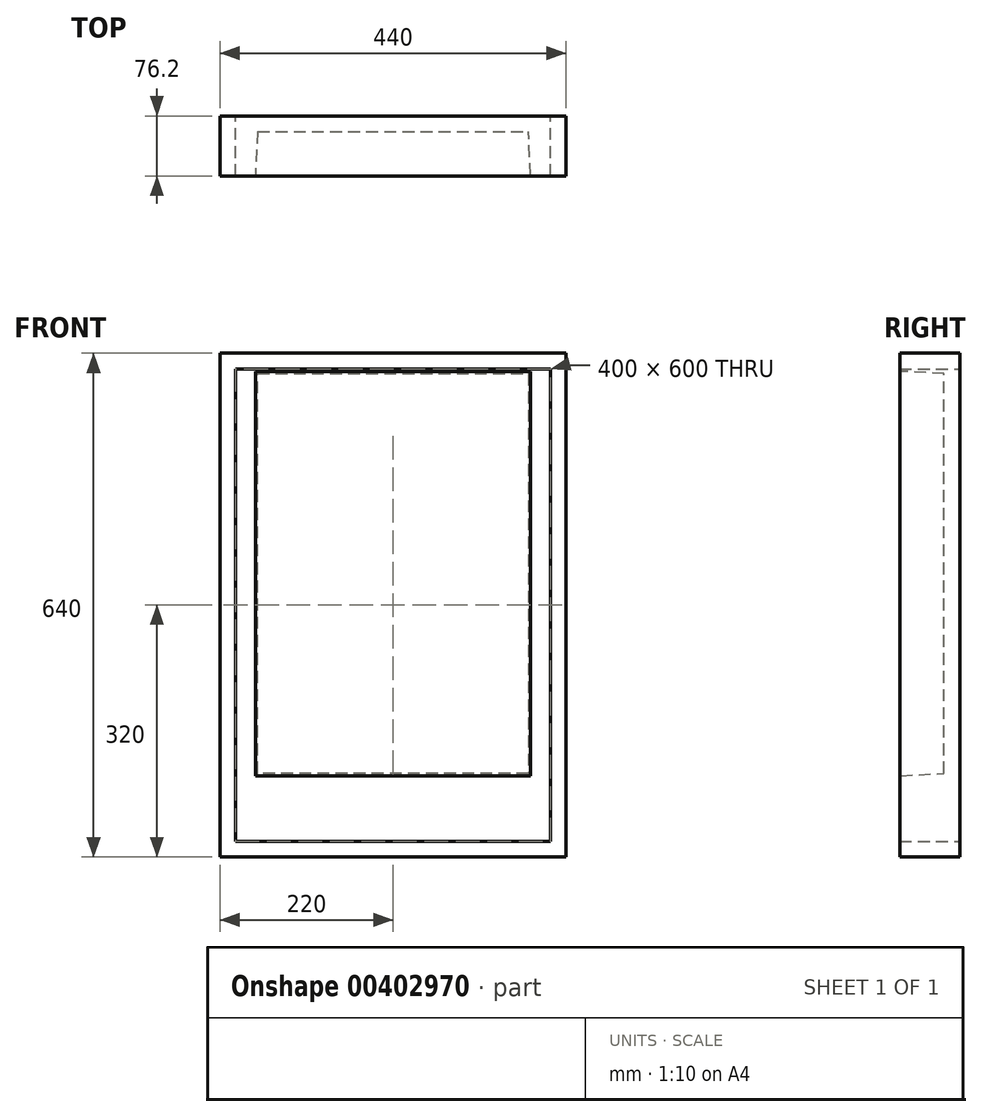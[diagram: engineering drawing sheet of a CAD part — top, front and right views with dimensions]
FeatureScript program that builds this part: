
annotation { "Feature Type Name" : "Feature", "Feature Type Description" : "" }
export const myFeature = defineFeature(function(context is Context, id is Id, definition is map)
    precondition{}
    {
        {
            var Q0;
            Q0=qCreatedBy(makeId("Front.planeOp"),FACE);
            var sketch = newSketch(context, id + "F0", { "sketchPlane" : qUnion([Q0])});
            skLineSegment(sketch, "E0.bottom", {"start": v(-220, 320) * mm, "end": v(220, 320) * mm});
            skLineSegment(sketch, "E0.top", {"start": v(-220, -320) * mm, "end": v(220, -320) * mm});
            skLineSegment(sketch, "E0.left", {"start": v(-220, 320) * mm, "end": v(-220, -320) * mm});
            skLineSegment(sketch, "E0.right", {"start": v(220, 320) * mm, "end": v(220, -320) * mm});
            skPoint(sketch, "E0.middle", {"position": v(0, 0) * mm});
            skLineSegment(sketch, "E1.0", {"start": v(-200, 300) * mm, "end": v(200, 300) * mm});
            skLineSegment(sketch, "E1.1", {"start": v(-200, 300) * mm, "end": v(-200, -300) * mm});
            skLineSegment(sketch, "E1.2", {"start": v(-200, -300) * mm, "end": v(200, -300) * mm});
            skLineSegment(sketch, "E1.3", {"start": v(200, 300) * mm, "end": v(200, -300) * mm});
            skSolve(sketch);
        }
        {
            var Q0;
            Q0=makeQuery(id+"F0.imprint","IMPRINT",FACE,{"disambiguationData":[TD([[makeQuery(id+"F0.imprint","IMPRINT",EDGE,{"derivedFrom":sQuery(id+"F0.wireOp",EDGE,"E0.bottom")}),-1.0]])]});
            extrude(context, id + "F1", {"entities" : qUnion([Q0]), "depth" : 76.2 * mm});
        }
        {
            var Q0;
            Q0=qCreatedBy(makeId("Front.planeOp"),FACE);
            var sketch = newSketch(context, id + "F2", { "sketchPlane" : qUnion([Q0])});
            skLineSegment(sketch, "E2.bottom", {"start": v(-172, 254) * mm, "end": v(172, 254) * mm});
            skLineSegment(sketch, "E2.top", {"start": v(-172, -254) * mm, "end": v(172, -254) * mm});
            skLineSegment(sketch, "E2.left", {"start": v(-172, 254) * mm, "end": v(-172, -254) * mm});
            skLineSegment(sketch, "E2.right", {"start": v(172, 254) * mm, "end": v(172, -254) * mm});
            skPoint(sketch, "E2.middle", {"position": v(0, 0) * mm});
            skSolve(sketch);
        }
        {
            var Q0;
            Q0 = qSketchRegion(id + "F2", true);
            extrude(context, id + "F3", {"entities" : qUnion([Q0]), "depth" : 55 * mm, "hasDraft" : true, "draftAngle" : 3 * degree});
        }
        {
            var Q0;
            Q0=makeQuery(id+"F3.opExtrude","SWEPT_BODY",BODY,{"disambiguationData":[OSD([sQuery(id+"F2.wireOp",EDGE,"E2.bottom"),sQuery(id+"F2.wireOp",EDGE,"E2.top"),sQuery(id+"F2.wireOp",EDGE,"E2.left"),sQuery(id+"F2.wireOp",EDGE,"E2.right")])]});
            transform(context, id + "F4", {"entities" : qUnion([Q0]), "transformType" : TransformType.TRANSLATION_3D, "dx" : 0 * mm, "dy" : -20 * mm, "dz" : 40 * mm, "makeCopy" : false});
        }
    });
